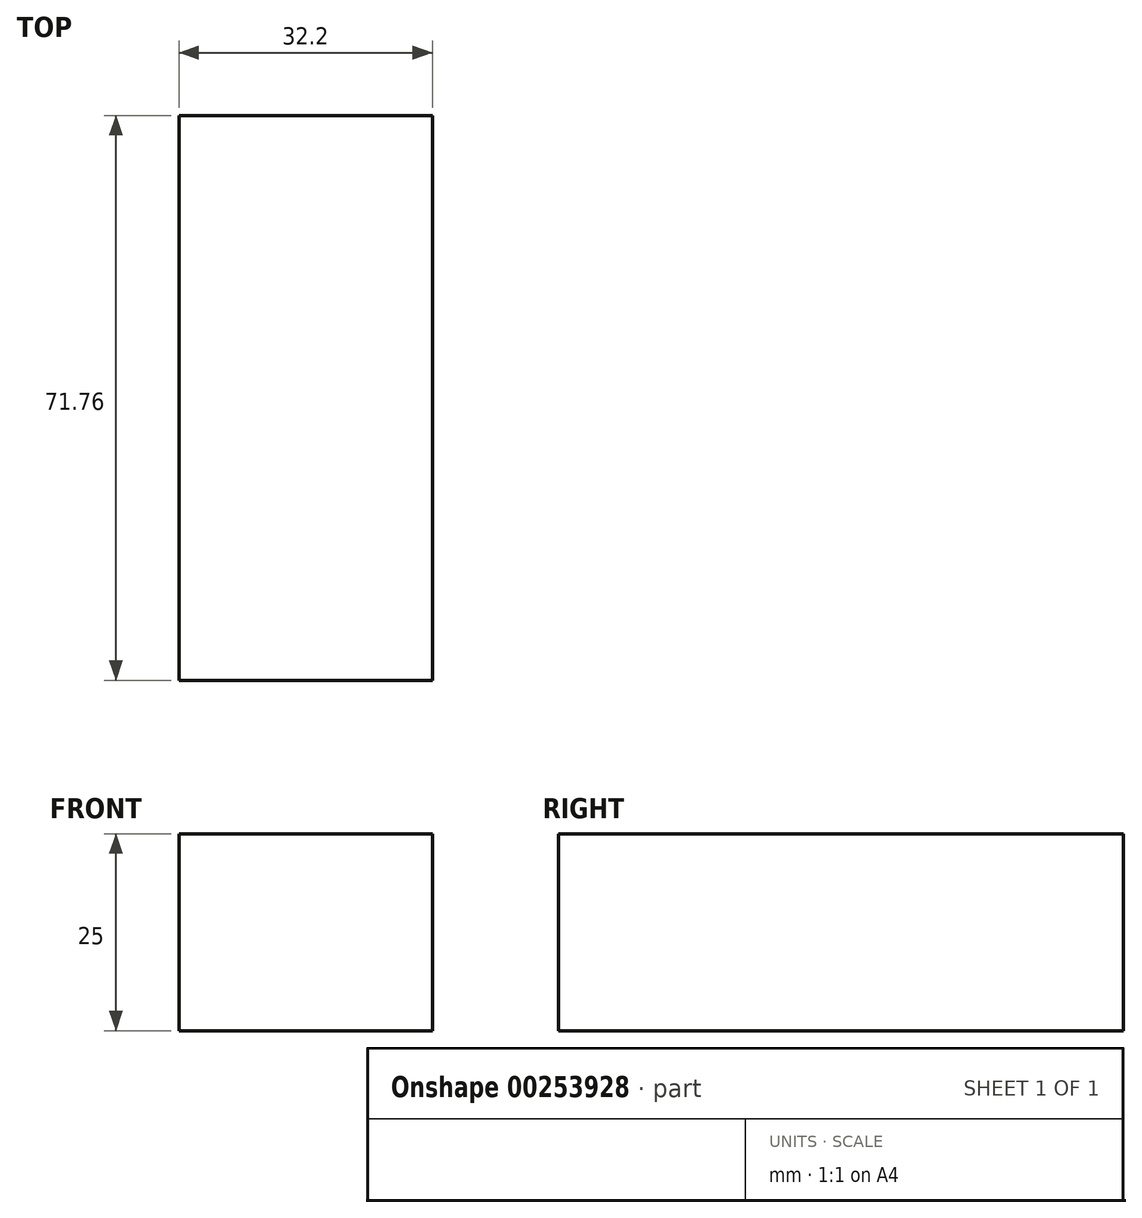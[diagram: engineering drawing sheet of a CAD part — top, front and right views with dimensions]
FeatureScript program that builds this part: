
annotation { "Feature Type Name" : "Feature", "Feature Type Description" : "" }
export const myFeature = defineFeature(function(context is Context, id is Id, definition is map)
    precondition{}
    {
        {
            var Q0;
            Q0=qCreatedBy(makeId("Top.planeOp"),FACE);
            var sketch = newSketch(context, id + "F0", { "sketchPlane" : qUnion([Q0])});
            skLineSegment(sketch, "E0.bottom", {"start": v(36.46, 9.06) * mm, "end": v(4.26, 9.06) * mm});
            skLineSegment(sketch, "E0.top", {"start": v(36.46, 80.82) * mm, "end": v(4.26, 80.82) * mm});
            skLineSegment(sketch, "E0.left", {"start": v(36.46, 9.06) * mm, "end": v(36.46, 80.82) * mm});
            skLineSegment(sketch, "E0.right", {"start": v(4.26, 9.06) * mm, "end": v(4.26, 80.82) * mm});
            skPoint(sketch, "E0.middle", {"position": v(20.36, 44.94) * mm});
            skSolve(sketch);
        }
        {
            var Q0;
            Q0=makeQuery(id+"F0.imprint","IMPRINT",FACE,{"disambiguationData":[TD([[makeQuery(id+"F0.imprint","IMPRINT",EDGE,{"derivedFrom":sQuery(id+"F0.wireOp",EDGE,"E0.bottom")}),-1.0]])]});
            extrude(context, id + "F1", {"entities" : qUnion([Q0]), "depth" : 25 * mm});
        }
    });
